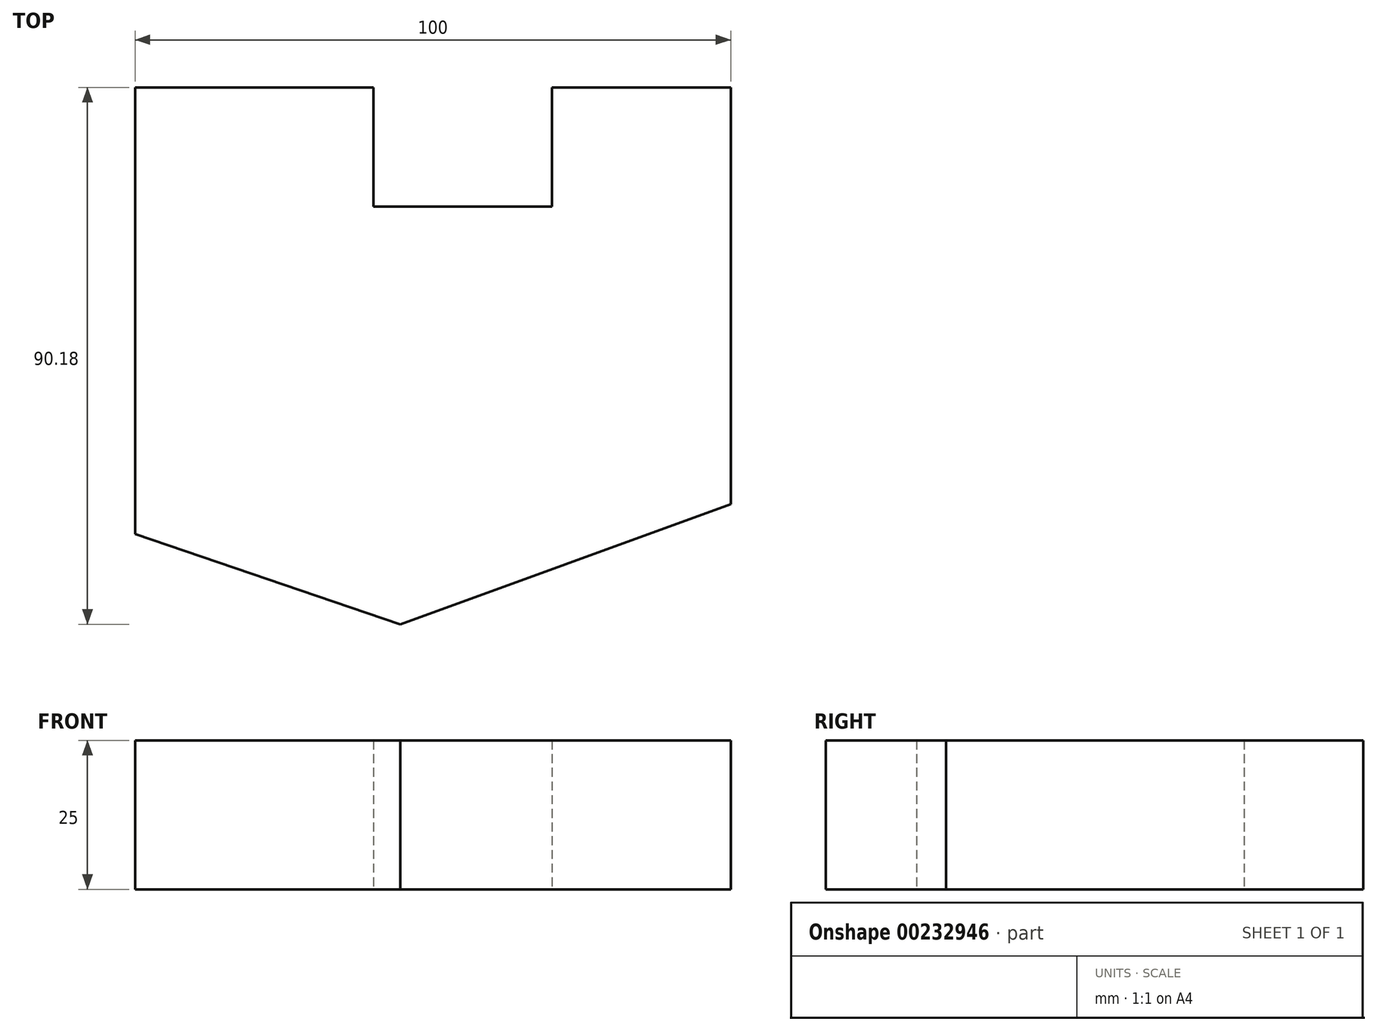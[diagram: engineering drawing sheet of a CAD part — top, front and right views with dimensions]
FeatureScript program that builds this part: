
annotation { "Feature Type Name" : "Feature", "Feature Type Description" : "" }
export const myFeature = defineFeature(function(context is Context, id is Id, definition is map)
    precondition{}
    {
        {
            var Q0;
            Q0=qCreatedBy(makeId("Top.planeOp"),FACE);
            var sketch = newSketch(context, id + "F0", { "sketchPlane" : qUnion([Q0])});
            skLineSegment(sketch, "E0", {"start": v(-70, 108.35) * mm, "end": v(-70, 33.35) * mm});
            skLineSegment(sketch, "E1", {"start": v(-70, 108.35) * mm, "end": v(-30, 108.35) * mm});
            skLineSegment(sketch, "E2", {"start": v(-30, 108.35) * mm, "end": v(-30, 88.35) * mm});
            skLineSegment(sketch, "E3", {"start": v(-30, 88.35) * mm, "end": v(0, 88.35) * mm});
            skLineSegment(sketch, "E4", {"start": v(0, 88.35) * mm, "end": v(0, 108.35) * mm});
            skLineSegment(sketch, "E5", {"start": v(0, 108.35) * mm, "end": v(30, 108.35) * mm});
            skLineSegment(sketch, "E6", {"start": v(30, 108.35) * mm, "end": v(30, 38.35) * mm});
            skLineSegment(sketch, "E7", {"start": v(30, 38.35) * mm, "end": v(-25.44, 18.17) * mm});
            skLineSegment(sketch, "E8", {"start": v(-25.44, 18.17) * mm, "end": v(-70, 33.35) * mm});
            skSolve(sketch);
        }
        {
            var Q0;
            Q0=makeQuery(id+"F0.imprint","IMPRINT",FACE,{"disambiguationData":[TD([[makeQuery(id+"F0.imprint","IMPRINT",EDGE,{"derivedFrom":sQuery(id+"F0.wireOp",EDGE,"E0")}),1.0]])]});
            extrude(context, id + "F1", {"entities" : qUnion([Q0]), "depth" : 25 * mm});
        }
    });
